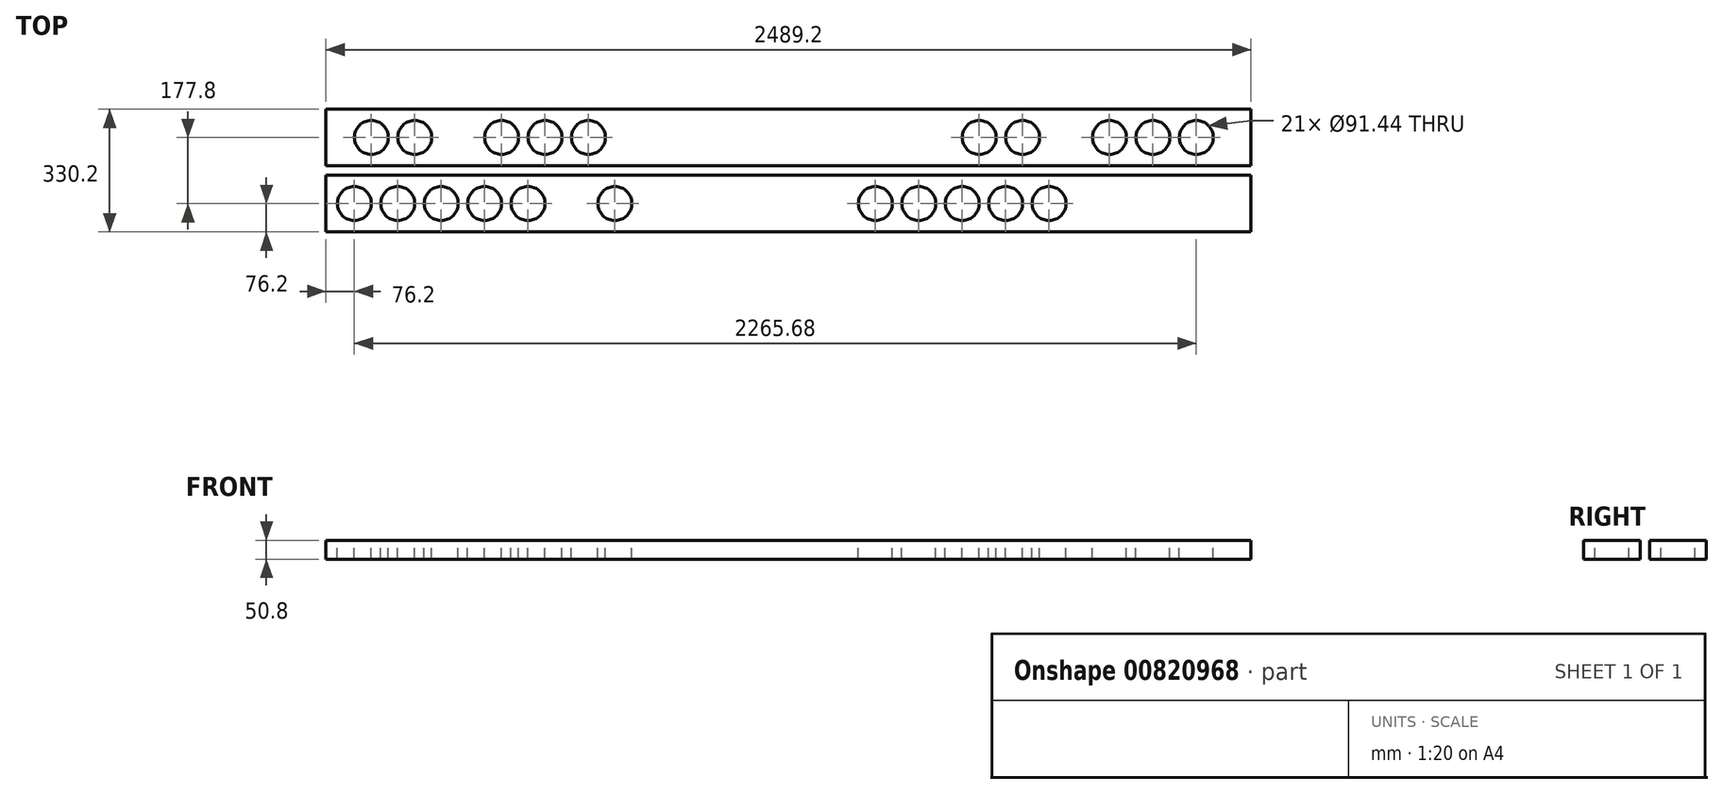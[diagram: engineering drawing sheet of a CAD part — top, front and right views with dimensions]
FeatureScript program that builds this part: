
annotation { "Feature Type Name" : "Feature", "Feature Type Description" : "" }
export const myFeature = defineFeature(function(context is Context, id is Id, definition is map)
    precondition{}
    {
        {
            var Q0;
            Q0=qCreatedBy(makeId("Right.planeOp"),FACE);
            var sketch = newSketch(context, id + "F0", { "sketchPlane" : qUnion([Q0])});
            skLineSegment(sketch, "E0.bottom", {"start": v(-76.2, 0) * mm, "end": v(76.2, 0) * mm});
            skLineSegment(sketch, "E0.top", {"start": v(-76.2, -50.8) * mm, "end": v(76.2, -50.8) * mm});
            skLineSegment(sketch, "E0.left", {"start": v(-76.2, 0) * mm, "end": v(-76.2, -50.8) * mm});
            skLineSegment(sketch, "E0.right", {"start": v(76.2, 0) * mm, "end": v(76.2, -50.8) * mm});
            skPoint(sketch, "E1.orphan", {"position": v(-76.4, 0) * mm});
            skLineSegment(sketch, "E2.MirrorCS", {"start": v(101.6, 0) * mm, "end": v(101.6, -50.8) * mm});
            skLineSegment(sketch, "E3.MirrorCS", {"start": v(254, 0) * mm, "end": v(101.6, 0) * mm});
            skLineSegment(sketch, "E4.MirrorCS", {"start": v(254, -50.8) * mm, "end": v(101.6, -50.8) * mm});
            skLineSegment(sketch, "E5.MirrorCS", {"start": v(254, 0) * mm, "end": v(254, -50.8) * mm});
            skSolve(sketch);
        }
        {
            var Q0;
            Q0=makeQuery(id+"F0.imprint","IMPRINT",FACE,{"disambiguationData":[TD([[makeQuery(id+"F0.imprint","IMPRINT",EDGE,{"derivedFrom":sQuery(id+"F0.wireOp",EDGE,"E0.bottom")}),-1.0]])]});
            var Q1;
            Q1=makeQuery(id+"F0.imprint","IMPRINT",FACE,{"disambiguationData":[TD([[makeQuery(id+"F0.imprint","IMPRINT",EDGE,{"derivedFrom":sQuery(id+"F0.wireOp",EDGE,"E2.MirrorCS")}),1.0]])]});
            extrude(context, id + "F1", {"entities" : qUnion([Q0, Q1]), "depth" : 2489.2 * mm, "offsetDistance" : 25.4 * mm});
        }
        {
            var Q0;
            Q0=qCreatedBy(makeId("Top.planeOp"),FACE);
            var sketch = newSketch(context, id + "F2", { "sketchPlane" : qUnion([Q0])});
            skCircle(sketch, "E6", {"center": v(76.2, 0) * mm, "radius": 45.72 * mm});
            skCircle(sketch, "E7", {"center": v(193.04, 0) * mm, "radius": 45.72 * mm});
            skCircle(sketch, "E8", {"center": v(309.88, 0) * mm, "radius": 45.72 * mm});
            skCircle(sketch, "E9", {"center": v(426.72, 0) * mm, "radius": 45.72 * mm});
            skCircle(sketch, "E10", {"center": v(543.56, 0) * mm, "radius": 45.72 * mm});
            skCircle(sketch, "E11", {"center": v(660.4, 0) * mm, "radius": 45.72 * mm});
            skCircle(sketch, "E12.MirrorC", {"center": v(777.24, 0) * mm, "radius": 45.72 * mm});
            skCircle(sketch, "E13.MirrorC", {"center": v(894.08, 0) * mm, "radius": 45.72 * mm});
            skCircle(sketch, "E14.MirrorC", {"center": v(1010.92, 0) * mm, "radius": 45.72 * mm});
            skCircle(sketch, "E15.MirrorC", {"center": v(1127.76, 0) * mm, "radius": 45.72 * mm});
            skCircle(sketch, "E16.MirrorC", {"center": v(1244.6, 0) * mm, "radius": 45.72 * mm});
            skCircle(sketch, "E17.MirrorC", {"center": v(1361.44, 0) * mm, "radius": 45.72 * mm});
            skPoint(sketch, "E18.orphan", {"position": v(817.88, 87.4) * mm});
            skCircle(sketch, "E19.MirrorC", {"center": v(1595.12, 0) * mm, "radius": 45.72 * mm});
            skCircle(sketch, "E20.MirrorC", {"center": v(1711.96, 0) * mm, "radius": 45.72 * mm});
            skCircle(sketch, "E21.MirrorC", {"center": v(1828.8, 0) * mm, "radius": 45.72 * mm});
            skCircle(sketch, "E22.MirrorC", {"center": v(1945.64, 0) * mm, "radius": 45.72 * mm});
            skCircle(sketch, "E23.MirrorC", {"center": v(2062.48, 0) * mm, "radius": 45.72 * mm});
            skCircle(sketch, "E24.MirrorC", {"center": v(1478.28, 0) * mm, "radius": 45.72 * mm});
            skCircle(sketch, "E25.MirrorC", {"center": v(2179.32, 0) * mm, "radius": 45.72 * mm});
            skCircle(sketch, "E26.MirrorC", {"center": v(2296.16, 0) * mm, "radius": 45.72 * mm});
            skCircle(sketch, "E27.MirrorC", {"center": v(2413, 0) * mm, "radius": 45.72 * mm});
            skPoint(sketch, "E28.orphan", {"position": v(1635.76, 75.64) * mm});
            skPoint(sketch, "E29.orphan", {"position": v(0, 212.92) * mm});
            skPoint(sketch, "E30.start.orphan", {"position": v(0, 0) * mm});
            skPoint(sketch, "E31.trimOffspring.end.orphan", {"position": v(817.88, 0) * mm});
            skPoint(sketch, "E32.MirrorCS.start.orphan", {"position": v(1635.76, 0) * mm});
            skPoint(sketch, "E33.MirrorCS.start.orphan", {"position": v(1621.08, 0) * mm});
            skPoint(sketch, "E34.trimOffspring.end.orphan", {"position": v(2438.96, 0) * mm});
            skPoint(sketch, "E35.orphan", {"position": v(0, 177.8) * mm});
            skPoint(sketch, "E36.MirrorCS.end.orphan", {"position": v(817.88, 177.8) * mm});
            skPoint(sketch, "E37.MirrorCS.start.orphan", {"position": v(1635.76, 177.8) * mm});
            skCircle(sketch, "E38", {"center": v(121.92, 177.8) * mm, "radius": 45.72 * mm});
            skCircle(sketch, "E39", {"center": v(238.76, 177.8) * mm, "radius": 45.72 * mm});
            skCircle(sketch, "E40", {"center": v(472.44, 177.8) * mm, "radius": 45.72 * mm});
            skCircle(sketch, "E41", {"center": v(589.28, 177.8) * mm, "radius": 45.72 * mm});
            skCircle(sketch, "E42", {"center": v(706.12, 177.8) * mm, "radius": 45.72 * mm});
            skCircle(sketch, "E43.MirrorC", {"center": v(929.64, 177.8) * mm, "radius": 45.72 * mm});
            skCircle(sketch, "E44.MirrorC", {"center": v(1046.48, 177.8) * mm, "radius": 45.72 * mm});
            skCircle(sketch, "E45.MirrorC", {"center": v(1397, 177.8) * mm, "radius": 45.72 * mm});
            skCircle(sketch, "E46.MirrorC", {"center": v(1513.84, 177.8) * mm, "radius": 45.72 * mm});
            skCircle(sketch, "E47.MirrorC", {"center": v(1280.16, 177.8) * mm, "radius": 45.72 * mm});
            skCircle(sketch, "E48.MirrorC", {"center": v(1757.68, 177.8) * mm, "radius": 45.72 * mm});
            skCircle(sketch, "E49.MirrorC", {"center": v(1874.52, 177.8) * mm, "radius": 45.72 * mm});
            skCircle(sketch, "E50.MirrorC", {"center": v(2108.2, 177.8) * mm, "radius": 45.72 * mm});
            skCircle(sketch, "E51.MirrorC", {"center": v(2225.04, 177.8) * mm, "radius": 45.72 * mm});
            skCircle(sketch, "E52.MirrorC", {"center": v(2341.88, 177.8) * mm, "radius": 45.72 * mm});
            skPoint(sketch, "E53.orphan", {"position": v(1635.76, 279.9) * mm});
            skPoint(sketch, "E54.orphan", {"position": v(817.88, 287.73) * mm});
            skSolve(sketch);
        }
        {
            var Q0;
            {var subQ0=sQuery(id+"F2.wireOp",EDGE,"E30");var subQ1=sQuery(id+"F2.wireOp",EDGE,"E6");var subQ2=makeQuery(id+"F2.imprint","INTERSECT",VERTEX,{"disambiguationData":[OD(0.0)],"derivedFrom":[subQ1,subQ0]});Q0=makeQuery(id+"F2.imprint","IMPRINT",FACE,{"disambiguationData":[TD([[makeQuery(id+"F2.imprint","IMPRINT",EDGE,{"disambiguationData":[TD([[subQ2,-1.0]])],"derivedFrom":subQ1}),1.0]])]});}
            var Q1;
            Q1=makeQuery(id+"F2.imprint","IMPRINT",FACE,{"disambiguationData":[TD([[makeQuery(id+"F2.imprint","IMPRINT",EDGE,{"derivedFrom":sQuery(id+"F2.wireOp",EDGE,"E27.MirrorC")}),-1.0]])]});
            var Q2;
            {var subQ0=sQuery(id+"F2.wireOp",EDGE,"E30");var subQ1=sQuery(id+"F2.wireOp",EDGE,"E7");var subQ2=makeQuery(id+"F2.imprint","INTERSECT",VERTEX,{"disambiguationData":[OD(0.0)],"derivedFrom":[subQ1,subQ0]});Q2=makeQuery(id+"F2.imprint","IMPRINT",FACE,{"disambiguationData":[TD([[makeQuery(id+"F2.imprint","IMPRINT",EDGE,{"disambiguationData":[TD([[subQ2,1.0]])],"derivedFrom":subQ1}),1.0]])]});}
            var Q3;
            {var subQ0=sQuery(id+"F2.wireOp",EDGE,"E30");var subQ1=sQuery(id+"F2.wireOp",EDGE,"E6");var subQ2=makeQuery(id+"F2.imprint","INTERSECT",VERTEX,{"disambiguationData":[OD(0.0)],"derivedFrom":[subQ1,subQ0]});Q3=makeQuery(id+"F2.imprint","IMPRINT",FACE,{"disambiguationData":[TD([[makeQuery(id+"F2.imprint","IMPRINT",EDGE,{"disambiguationData":[TD([[subQ2,1.0]])],"derivedFrom":subQ1}),1.0]])]});}
            var Q4;
            {var subQ0=sQuery(id+"F2.wireOp",EDGE,"E30");var subQ1=sQuery(id+"F2.wireOp",EDGE,"E7");var subQ2=makeQuery(id+"F2.imprint","INTERSECT",VERTEX,{"disambiguationData":[OD(0.0)],"derivedFrom":[subQ1,subQ0]});Q4=makeQuery(id+"F2.imprint","IMPRINT",FACE,{"disambiguationData":[TD([[makeQuery(id+"F2.imprint","IMPRINT",EDGE,{"disambiguationData":[TD([[subQ2,-1.0]])],"derivedFrom":subQ1}),1.0]])]});}
            var Q5;
            Q5=makeQuery(id+"F2.imprint","IMPRINT",FACE,{"disambiguationData":[TD([[makeQuery(id+"F2.imprint","IMPRINT",EDGE,{"derivedFrom":sQuery(id+"F2.wireOp",EDGE,"E8")}),1.0]])]});
            var Q6;
            Q6=makeQuery(id+"F2.imprint","IMPRINT",FACE,{"disambiguationData":[TD([[makeQuery(id+"F2.imprint","IMPRINT",EDGE,{"derivedFrom":sQuery(id+"F2.wireOp",EDGE,"E9")}),1.0]])]});
            var Q7;
            Q7=makeQuery(id+"F2.imprint","IMPRINT",FACE,{"disambiguationData":[TD([[makeQuery(id+"F2.imprint","IMPRINT",EDGE,{"derivedFrom":sQuery(id+"F2.wireOp",EDGE,"E10")}),1.0]])]});
            var Q8;
            Q8=makeQuery(id+"F2.imprint","IMPRINT",FACE,{"disambiguationData":[TD([[makeQuery(id+"F2.imprint","IMPRINT",EDGE,{"derivedFrom":sQuery(id+"F2.wireOp",EDGE,"E11")}),-1.0]])]});
            var Q9;
            Q9=makeQuery(id+"F2.imprint","IMPRINT",FACE,{"disambiguationData":[TD([[makeQuery(id+"F2.imprint","IMPRINT",EDGE,{"derivedFrom":sQuery(id+"F2.wireOp",EDGE,"E12.MirrorC")}),1.0]])]});
            var Q10;
            Q10=makeQuery(id+"F2.imprint","IMPRINT",FACE,{"disambiguationData":[TD([[makeQuery(id+"F2.imprint","IMPRINT",EDGE,{"derivedFrom":sQuery(id+"F2.wireOp",EDGE,"E13.MirrorC")}),-1.0]])]});
            var Q11;
            Q11=makeQuery(id+"F2.imprint","IMPRINT",FACE,{"disambiguationData":[TD([[makeQuery(id+"F2.imprint","IMPRINT",EDGE,{"derivedFrom":sQuery(id+"F2.wireOp",EDGE,"E17.MirrorC")}),-1.0]])]});
            var Q12;
            Q12=makeQuery(id+"F2.imprint","IMPRINT",FACE,{"disambiguationData":[TD([[makeQuery(id+"F2.imprint","IMPRINT",EDGE,{"derivedFrom":sQuery(id+"F2.wireOp",EDGE,"E16.MirrorC")}),-1.0]])]});
            var Q13;
            Q13=makeQuery(id+"F2.imprint","IMPRINT",FACE,{"disambiguationData":[TD([[makeQuery(id+"F2.imprint","IMPRINT",EDGE,{"derivedFrom":sQuery(id+"F2.wireOp",EDGE,"E20.MirrorC")}),1.0]])]});
            var Q14;
            Q14=makeQuery(id+"F2.imprint","IMPRINT",FACE,{"disambiguationData":[TD([[makeQuery(id+"F2.imprint","IMPRINT",EDGE,{"derivedFrom":sQuery(id+"F2.wireOp",EDGE,"E21.MirrorC")}),1.0]])]});
            var Q15;
            Q15=makeQuery(id+"F2.imprint","IMPRINT",FACE,{"disambiguationData":[TD([[makeQuery(id+"F2.imprint","IMPRINT",EDGE,{"derivedFrom":sQuery(id+"F2.wireOp",EDGE,"E15.MirrorC")}),-1.0]])]});
            var Q16;
            Q16=makeQuery(id+"F2.imprint","IMPRINT",FACE,{"disambiguationData":[TD([[makeQuery(id+"F2.imprint","IMPRINT",EDGE,{"derivedFrom":sQuery(id+"F2.wireOp",EDGE,"E14.MirrorC")}),-1.0]])]});
            var Q17;
            Q17=makeQuery(id+"F2.imprint","IMPRINT",FACE,{"disambiguationData":[TD([[makeQuery(id+"F2.imprint","IMPRINT",EDGE,{"derivedFrom":sQuery(id+"F2.wireOp",EDGE,"E24.MirrorC")}),1.0]])]});
            var Q18;
            Q18=makeQuery(id+"F2.imprint","IMPRINT",FACE,{"disambiguationData":[TD([[makeQuery(id+"F2.imprint","IMPRINT",EDGE,{"derivedFrom":sQuery(id+"F2.wireOp",EDGE,"E19.MirrorC")}),1.0]])]});
            var Q19;
            Q19=makeQuery(id+"F2.imprint","IMPRINT",FACE,{"disambiguationData":[TD([[makeQuery(id+"F2.imprint","IMPRINT",EDGE,{"derivedFrom":sQuery(id+"F2.wireOp",EDGE,"E22.MirrorC")}),1.0]])]});
            var Q20;
            Q20=makeQuery(id+"F2.imprint","IMPRINT",FACE,{"disambiguationData":[TD([[makeQuery(id+"F2.imprint","IMPRINT",EDGE,{"derivedFrom":sQuery(id+"F2.wireOp",EDGE,"E23.MirrorC")}),-1.0]])]});
            var Q21;
            Q21=makeQuery(id+"F2.imprint","IMPRINT",FACE,{"disambiguationData":[TD([[makeQuery(id+"F2.imprint","IMPRINT",EDGE,{"derivedFrom":sQuery(id+"F2.wireOp",EDGE,"E25.MirrorC")}),-1.0]])]});
            var Q22;
            Q22=makeQuery(id+"F2.imprint","IMPRINT",FACE,{"disambiguationData":[TD([[makeQuery(id+"F2.imprint","IMPRINT",EDGE,{"derivedFrom":sQuery(id+"F2.wireOp",EDGE,"E26.MirrorC")}),-1.0]])]});
            extrude(context, id + "F3", {"entities" : qUnion([Q0, Q1, Q2, Q3, Q4, Q5, Q6, Q7, Q8, Q9, Q10, Q11, Q12, Q13, Q14, Q15, Q16, Q17, Q18, Q19, Q20, Q21, Q22]), "operationType" : NewBodyOperationType.REMOVE, "oppositeDirection" : true, "depth" : 63.5 * mm, "offsetDistance" : 25.4 * mm});
        }
        {
            var Q0;
            Q0=makeQuery(id+"F2.imprint","IMPRINT",FACE,{"disambiguationData":[TD([[makeQuery(id+"F2.imprint","IMPRINT",EDGE,{"derivedFrom":sQuery(id+"F2.wireOp",EDGE,"E38")}),1.0]])]});
            var Q1;
            Q1=makeQuery(id+"F2.imprint","IMPRINT",FACE,{"disambiguationData":[TD([[makeQuery(id+"F2.imprint","IMPRINT",EDGE,{"derivedFrom":sQuery(id+"F2.wireOp",EDGE,"E39")}),1.0]])]});
            var Q2;
            Q2=makeQuery(id+"F2.imprint","IMPRINT",FACE,{"disambiguationData":[TD([[makeQuery(id+"F2.imprint","IMPRINT",EDGE,{"derivedFrom":sQuery(id+"F2.wireOp",EDGE,"E40")}),1.0]])]});
            var Q3;
            Q3=makeQuery(id+"F2.imprint","IMPRINT",FACE,{"disambiguationData":[TD([[makeQuery(id+"F2.imprint","IMPRINT",EDGE,{"derivedFrom":sQuery(id+"F2.wireOp",EDGE,"E41")}),1.0]])]});
            var Q4;
            Q4=makeQuery(id+"F2.imprint","IMPRINT",FACE,{"disambiguationData":[TD([[makeQuery(id+"F2.imprint","IMPRINT",EDGE,{"derivedFrom":sQuery(id+"F2.wireOp",EDGE,"E42")}),1.0]])]});
            var Q5;
            Q5=makeQuery(id+"F2.imprint","IMPRINT",FACE,{"disambiguationData":[TD([[makeQuery(id+"F2.imprint","IMPRINT",EDGE,{"derivedFrom":sQuery(id+"F2.wireOp",EDGE,"E43.MirrorC")}),-1.0]])]});
            var Q6;
            Q6=makeQuery(id+"F2.imprint","IMPRINT",FACE,{"disambiguationData":[TD([[makeQuery(id+"F2.imprint","IMPRINT",EDGE,{"derivedFrom":sQuery(id+"F2.wireOp",EDGE,"E44.MirrorC")}),-1.0]])]});
            var Q7;
            Q7=makeQuery(id+"F2.imprint","IMPRINT",FACE,{"disambiguationData":[TD([[makeQuery(id+"F2.imprint","IMPRINT",EDGE,{"derivedFrom":sQuery(id+"F2.wireOp",EDGE,"E47.MirrorC")}),-1.0]])]});
            var Q8;
            Q8=makeQuery(id+"F2.imprint","IMPRINT",FACE,{"disambiguationData":[TD([[makeQuery(id+"F2.imprint","IMPRINT",EDGE,{"derivedFrom":sQuery(id+"F2.wireOp",EDGE,"E45.MirrorC")}),-1.0]])]});
            var Q9;
            Q9=makeQuery(id+"F2.imprint","IMPRINT",FACE,{"disambiguationData":[TD([[makeQuery(id+"F2.imprint","IMPRINT",EDGE,{"derivedFrom":sQuery(id+"F2.wireOp",EDGE,"E46.MirrorC")}),-1.0]])]});
            var Q10;
            Q10=makeQuery(id+"F2.imprint","IMPRINT",FACE,{"disambiguationData":[TD([[makeQuery(id+"F2.imprint","IMPRINT",EDGE,{"derivedFrom":sQuery(id+"F2.wireOp",EDGE,"E48.MirrorC")}),1.0]])]});
            var Q11;
            Q11=makeQuery(id+"F2.imprint","IMPRINT",FACE,{"disambiguationData":[TD([[makeQuery(id+"F2.imprint","IMPRINT",EDGE,{"derivedFrom":sQuery(id+"F2.wireOp",EDGE,"E49.MirrorC")}),1.0]])]});
            var Q12;
            Q12=makeQuery(id+"F2.imprint","IMPRINT",FACE,{"disambiguationData":[TD([[makeQuery(id+"F2.imprint","IMPRINT",EDGE,{"derivedFrom":sQuery(id+"F2.wireOp",EDGE,"E52.MirrorC")}),1.0]])]});
            var Q13;
            Q13=makeQuery(id+"F2.imprint","IMPRINT",FACE,{"disambiguationData":[TD([[makeQuery(id+"F2.imprint","IMPRINT",EDGE,{"derivedFrom":sQuery(id+"F2.wireOp",EDGE,"E51.MirrorC")}),1.0]])]});
            var Q14;
            Q14=makeQuery(id+"F2.imprint","IMPRINT",FACE,{"disambiguationData":[TD([[makeQuery(id+"F2.imprint","IMPRINT",EDGE,{"derivedFrom":sQuery(id+"F2.wireOp",EDGE,"E50.MirrorC")}),1.0]])]});
            extrude(context, id + "F4", {"entities" : qUnion([Q0, Q1, Q2, Q3, Q4, Q5, Q6, Q7, Q8, Q9, Q10, Q11, Q12, Q13, Q14]), "operationType" : NewBodyOperationType.REMOVE, "oppositeDirection" : true, "depth" : 63.5 * mm, "offsetDistance" : 25.4 * mm});
        }
    });
